# Revit family: TESK_Насос вертикальный_SVM(T)-90
name_source: partatom
category: Оборудование
units: mm (PartAtom-declared; Revit-internal decimal feet)

## family parameters
Всегда вертикально = Да
Классификация = Насос
На основе рабочей плоскости = Нет
Общий = Нет
При загрузке вырезать с полостями = Нет
Размер круглого соединителя = Использовать диаметр
Тип детали = Вставляется
Точка расчета площади = Нет

## types (24) — shared parameters
ADSK_Версия Revit = 2019
ADSK_Версия семейства = 1.0
ADSK_Диаметр условный = 100 мм
ADSK_Единица измерения = шт.
ADSK_Завод-изготовитель = TESK
ADSK_Классификация нагрузок = Прочее
ADSK_Количество = 1
ADSK_Количество фаз = 3
ADSK_Количество фаз числовое = 3
ADSK_Коэффициент мощности = 1
ADSK_Наименование краткое = Вертикальный многоступенчатый центробежный насос
ADSK_Напряжение = 400 В
URL = www.teskpump.ru
Материал_1 = TESK_Черный_Условный
Материал_2 = TESK_Нержавеющая сталь
Материал_КорпусДвигателя = TESK_Черный_Ребра_Условный
Таблица_Поиска = TESK_SVM(T)-90
УГО_Длина = 380 мм
Фланец_Толщина = 26 мм

## per-type parameters (varying)
| type | ADSK_Код изделия | ADSK_Масса | ADSK_Масса_Текст | ADSK_Наименование | ADSK_Номинальная мощность | ADSK_Полная мощность | D_Башня | Высота_Башня | Высота_Корпуса | Двигатель_Высота | Двигатель_ОтступКоробки | Двигатель_Ширина | Материал_КорпусУлитка | Напор максимальный | Толщина_ФланцаДвигателя |
| SVM 90-1-1 5.5kW 3x380V 50Hz IE3 | 7790-10-10003380NSSF | 105 | 105 | Вертикальный многоступенчатый центробежный насос SVM, DN100, PN16, Hmax=22м (3x380V 50Hz IE3) | 6 кВт | 6 кВ·А | 195 мм | 200 мм | 571 мм | 435 мм | 208 мм | 260 мм | TESK_Нержавеющая сталь | 22 | 13 мм |
| SVM 90-1 7.5kW 3x380V 50Hz IE3 | 7790-100003380NSSF | 110 | 110 | Вертикальный многоступенчатый центробежный насос SVM, DN100, PN16, Hmax=25м (3x380V 50Hz IE3) | 8 кВт | 8 кВ·А | 195 мм | 200 мм | 571 мм | 435 мм | 208 мм | 260 мм | TESK_Нержавеющая сталь | 25 | 13 мм |
| SVM 90-2-2 11kW 3x380V 50Hz IE3 | 7790-2-20003380NSSF | 181 | 181 | Вертикальный многоступенчатый центробежный насос SVM, DN100, PN16, Hmax=41м (3x380V 50Hz IE3) | 11 кВт | 11 кВ·А | 263 мм | 240 мм | 773 мм | 580 мм | 260 мм | 350 мм | TESK_Нержавеющая сталь | 41 | 17 мм |
| SVM 90-2 15kW 3x380V 50Hz IE3 | 7790-200003380NSSF | 192 | 192 | Вертикальный многоступенчатый центробежный насос SVM, DN100, PN16, Hmax=53м (3x380V 50Hz IE3) | 15 кВт | 15 кВ·А | 263 мм | 240 мм | 773 мм | 580 мм | 260 мм | 350 мм | TESK_Нержавеющая сталь | 53 | 17 мм |
| SVM 90-3-2 18.5kW 3x380V 50Hz IE3 | 7790-30-20003380NSSF | 215 | 215 | Вертикальный многоступенчатый центробежный насос SVM, DN100, PN16, Hmax=68м (3x380V 50Hz IE3) | 19 кВт | 19 кВ·А | 263 мм | 300 мм | 865 мм | 610 мм | 260 мм | 350 мм | TESK_Нержавеющая сталь | 68 | 18 мм |
| SVM 90-3 22kW 3x380V 50Hz IE3 | 7790-300003380NSSF | 252 | 252 | Вертикальный многоступенчатый центробежный насос SVM, DN100, PN16, Hmax=81м (3x380V 50Hz IE3) | 22 кВт | 22 кВ·А | 270 мм | 300 мм | 865 мм | 645 мм | 285 мм | 360 мм | TESK_Нержавеющая сталь | 81 | 19 мм |
| SVM 90-4-2 30kW 3x380V 50Hz IE3 | 7790-40-20003380NSSF | 312 | 312 | Вертикальный многоступенчатый центробежный насос SVM, DN100, PN16, Hmax=98м (3x380V 50Hz IE3) | 30 кВт | 30 кВ·А | 300 мм | 320 мм | 957 мм | 705 мм | 310 мм | 400 мм | TESK_Нержавеющая сталь | 98 | 21 мм |
| SVM 90-4 30kW 3x380V 50Hz IE3 | 7790-40003380NSSF | 312 | 312 | Вертикальный многоступенчатый центробежный насос SVM, DN100, PN16, Hmax=110м (3x380V 50Hz IE3) | 30 кВт | 30 кВ·А | 300 мм | 320 мм | 957 мм | 705 мм | 310 мм | 400 мм | TESK_Нержавеющая сталь | 110 | 21 мм |
| SVM 90-5-2 37kW 3x380V 50Hz IE3 | 7790-50-20003380NSSF | 336 | 336 | Вертикальный многоступенчатый центробежный насос SVM, DN100, PN16, Hmax=126м (3x380V 50Hz IE3) | 37 кВт | 37 кВ·А | 300 мм | 340 мм | 1049 мм | 705 мм | 310 мм | 400 мм | TESK_Нержавеющая сталь | 126 | 21 мм |
| SVM 90-5 37kW 3x380V 50Hz IE3 | 7790-500003380NSSF | 336 | 336 | Вертикальный многоступенчатый центробежный насос SVM, DN100, PN16, Hmax=139м (3x380V 50Hz IE3) | 37 кВт | 37 кВ·А | 300 мм | 340 мм | 1049 мм | 705 мм | 310 мм | 400 мм | TESK_Нержавеющая сталь | 139 | 21 мм |
| SVM 90-6-2 45kW 3x380V 50Hz IE3 | 7790-60-20003380NSSF | 407 | 407 | Вертикальный многоступенчатый центробежный насос SVM, DN100, PN16, Hmax=155м (3x380V 50Hz IE3) | 45 кВт | 45 кВ·А | 345 мм | 380 мм | 1141 мм | 740 мм | 340 мм | 460 мм | TESK_Нержавеющая сталь | 155 | 22 мм |
| SVM 90-6 45kW 3x380V 50Hz IE3 | 7790-60-003380NSSF | 407 | 407 | Вертикальный многоступенчатый центробежный насос SVM, DN100, PN16, Hmax=168м (3x380V 50Hz IE3) | 45 кВт | 45 кВ·А | 345 мм | 380 мм | 1141 мм | 740 мм | 340 мм | 460 мм | TESK_Нержавеющая сталь | 168 | 22 мм |
| SVMT 90-1-1 5.5kW 3x380V 50Hz IE3 | 7790-10-10003380N | 105 | 105 | Вертикальный многоступенчатый центробежный насос SVMT, DN100, PN16, Hmax=22м (3x380V 50Hz IE3) | 6 кВт | 6 кВ·А | 195 мм | 200 мм | 571 мм | 435 мм | 208 мм | 260 мм | TESK_Черный_Условный | 22 | 13 мм |
| SVMT 90-1 7.5kW 3x380V 50Hz IE3 | 7790-100003380N | 110 | 110 | Вертикальный многоступенчатый центробежный насос SVMT, DN100, PN16, Hmax=25м (3x380V 50Hz IE3) | 8 кВт | 8 кВ·А | 195 мм | 200 мм | 571 мм | 435 мм | 208 мм | 260 мм | TESK_Черный_Условный | 25 | 13 мм |
| SVMT 90-2-2 11kW 3x380V 50Hz IE3 | 7790-2-20003380N | 181 | 181 | Вертикальный многоступенчатый центробежный насос SVMT, DN100, PN16, Hmax=41м (3x380V 50Hz IE3) | 11 кВт | 11 кВ·А | 263 мм | 240 мм | 773 мм | 580 мм | 260 мм | 350 мм | TESK_Черный_Условный | 41 | 17 мм |
| SVMT 90-2 15kW 3x380V 50Hz IE3 | 7790-200003380N | 192 | 192 | Вертикальный многоступенчатый центробежный насос SVMT, DN100, PN16, Hmax=53м (3x380V 50Hz IE3) | 15 кВт | 15 кВ·А | 263 мм | 240 мм | 773 мм | 580 мм | 260 мм | 350 мм | TESK_Черный_Условный | 53 | 17 мм |
| SVMT 90-3-2 18.5kW 3x380V 50Hz IE3 | 7790-30-20003380N | 215 | 215 | Вертикальный многоступенчатый центробежный насос SVMT, DN100, PN16, Hmax=68м (3x380V 50Hz IE3) | 19 кВт | 19 кВ·А | 263 мм | 300 мм | 865 мм | 610 мм | 260 мм | 350 мм | TESK_Черный_Условный | 68 | 18 мм |
| SVMT 90-3 22kW 3x380V 50Hz IE3 | 7790-300003380N | 252 | 252 | Вертикальный многоступенчатый центробежный насос SVMT, DN100, PN16, Hmax=81м (3x380V 50Hz IE3) | 22 кВт | 22 кВ·А | 270 мм | 300 мм | 865 мм | 645 мм | 285 мм | 360 мм | TESK_Черный_Условный | 81 | 19 мм |
| SVMT 90-4-2 30kW 3x380V 50Hz IE3 | 7790-40-20003380N | 312 | 312 | Вертикальный многоступенчатый центробежный насос SVMT, DN100, PN16, Hmax=98м (3x380V 50Hz IE3) | 30 кВт | 30 кВ·А | 300 мм | 320 мм | 957 мм | 705 мм | 310 мм | 400 мм | TESK_Черный_Условный | 98 | 21 мм |
| SVMT 90-4 30kW 3x380V 50Hz IE3 | 7790-40003380N | 312 | 312 | Вертикальный многоступенчатый центробежный насос SVMT, DN100, PN16, Hmax=110м (3x380V 50Hz IE3) | 30 кВт | 30 кВ·А | 300 мм | 320 мм | 957 мм | 705 мм | 310 мм | 400 мм | TESK_Черный_Условный | 110 | 21 мм |
| SVMT 90-5-2 37kW 3x380V 50Hz IE3 | 7790-50-20003380N | 336 | 336 | Вертикальный многоступенчатый центробежный насос SVMT, DN100, PN16, Hmax=126м (3x380V 50Hz IE3) | 37 кВт | 37 кВ·А | 300 мм | 340 мм | 1049 мм | 705 мм | 310 мм | 400 мм | TESK_Черный_Условный | 126 | 21 мм |
| SVMT 90-5 37kW 3x380V 50Hz IE3 | 7790-500003380N | 336 | 336 | Вертикальный многоступенчатый центробежный насос SVMT, DN100, PN16, Hmax=139м (3x380V 50Hz IE3) | 37 кВт | 37 кВ·А | 300 мм | 340 мм | 1049 мм | 705 мм | 310 мм | 400 мм | TESK_Черный_Условный | 139 | 21 мм |
| SVMT 90-6-2 45kW 3x380V 50Hz IE3 | 7790-60-20003380N | 407 | 407 | Вертикальный многоступенчатый центробежный насос SVMT, DN100, PN16, Hmax=155м (3x380V 50Hz IE3) | 45 кВт | 45 кВ·А | 345 мм | 380 мм | 1141 мм | 740 мм | 340 мм | 460 мм | TESK_Черный_Условный | 155 | 22 мм |
| SVMT 90-6 45kW 3x380V 50Hz IE3 | 7790-600003380N | 407 | 407 | Вертикальный многоступенчатый центробежный насос SVMT, DN100, PN16, Hmax=168м (3x380V 50Hz IE3) | 45 кВт | 45 кВ·А | 345 мм | 380 мм | 1141 мм | 740 мм | 340 мм | 460 мм | TESK_Черный_Условный | 168 | 22 мм |

note: column(s) folded — value = type name in every type: ADSK_Марка
